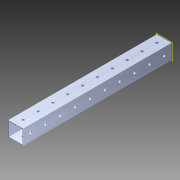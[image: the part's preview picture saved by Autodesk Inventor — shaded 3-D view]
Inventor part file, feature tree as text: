
AUTODESK INVENTOR PART (.ipt)
format: ipt  version: 2014 SP1 (Build 180222100, 222)  size: 1,161,728 bytes
history: native  units: in
note: dims shown in document units (in); Inventor stores cm internally (conversion verified against a paired STEP export)
features: pattern_circular x1, other x1, plane x1, extrude x1, imported_body x1, sketch x1
ambient origin geometry x8: Origin, YZ Plane, XZ Plane, XY Plane, X Axis, Y Axis, Z Axis, Center Point
bodies: Body1 (feature_tree)
feature tree (6):
  pattern_circular  "CirPattern2"
  other  "217-3426-STEP1"
  plane  "Work Plane1"
  extrude  "Extrusion1"  Depth=3937.0079in TaperAngle=0.0deg
  imported_body  "Base1"
  sketch  "Sketch1"  dims[d0=-10.0in d1=3937.0079in d2=0.0in]
